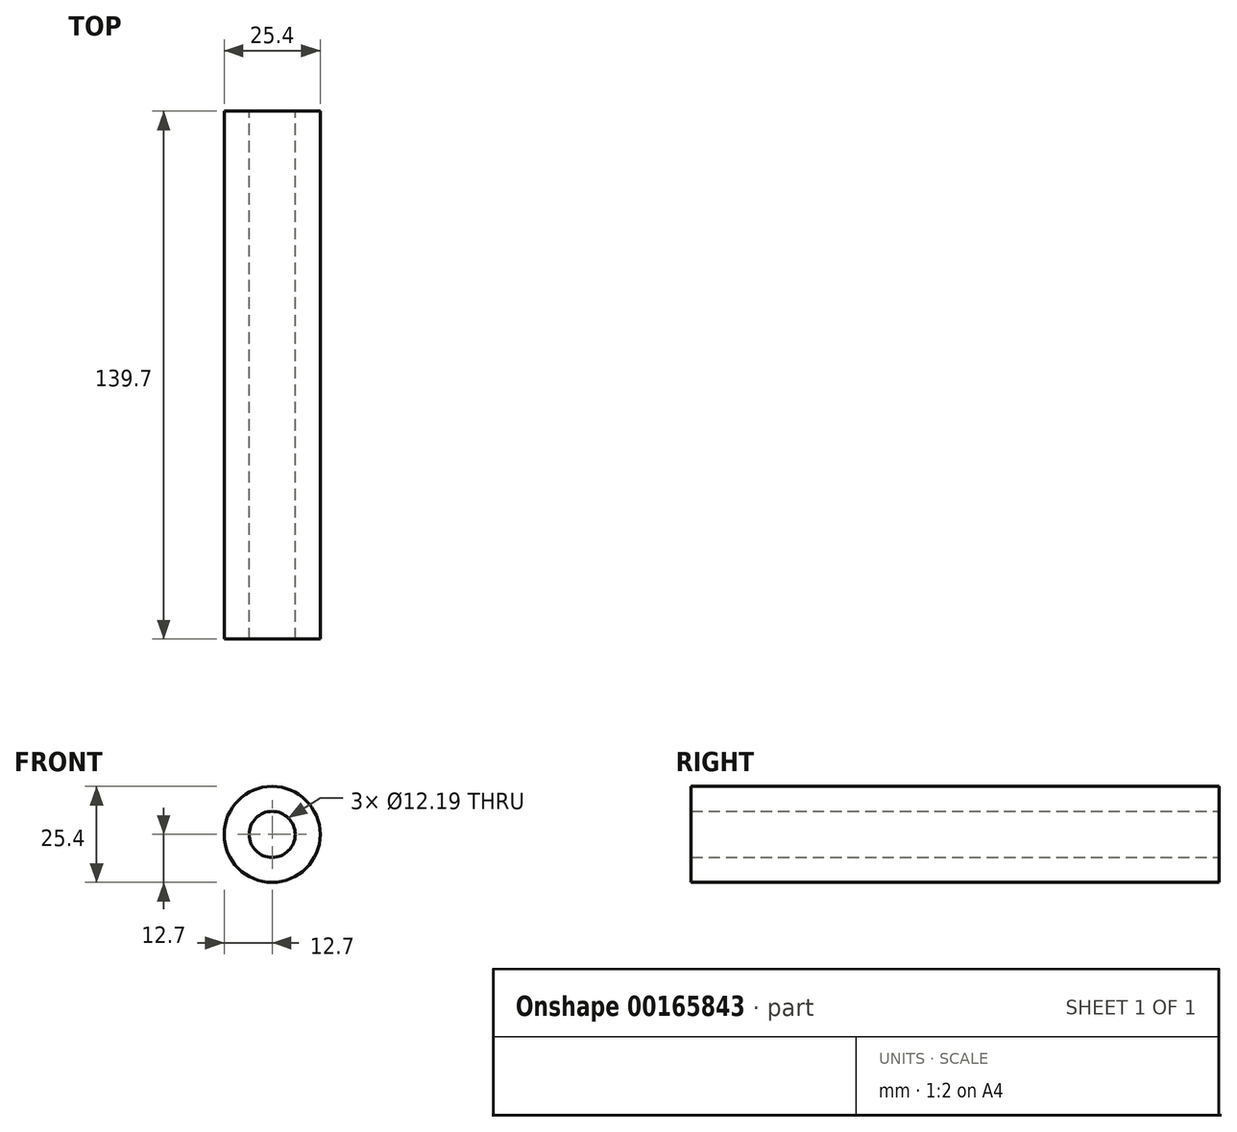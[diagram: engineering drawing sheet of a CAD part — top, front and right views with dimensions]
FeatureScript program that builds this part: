
annotation { "Feature Type Name" : "Feature", "Feature Type Description" : "" }
export const myFeature = defineFeature(function(context is Context, id is Id, definition is map)
    precondition{}
    {
        {
            var Q0;
            Q0=qCreatedBy(makeId("Front.planeOp"),FACE);
            var sketch = newSketch(context, id + "F0", { "sketchPlane" : qUnion([Q0])});
            skCircle(sketch, "E0", {"center": v(0, 0) * mm, "radius": 12.7 * mm});
            skCircle(sketch, "E1", {"center": v(0, 0) * mm, "radius": 6.1 * mm});
            skSolve(sketch);
        }
        {
            var Q0;
            Q0 = qSketchRegion(id + "F0", true);
            extrude(context, id + "F1", {"entities" : qUnion([Q0]), "endBound" : BoundingType.SYMMETRIC, "depth" : 139.7 * mm});
        }
    });
